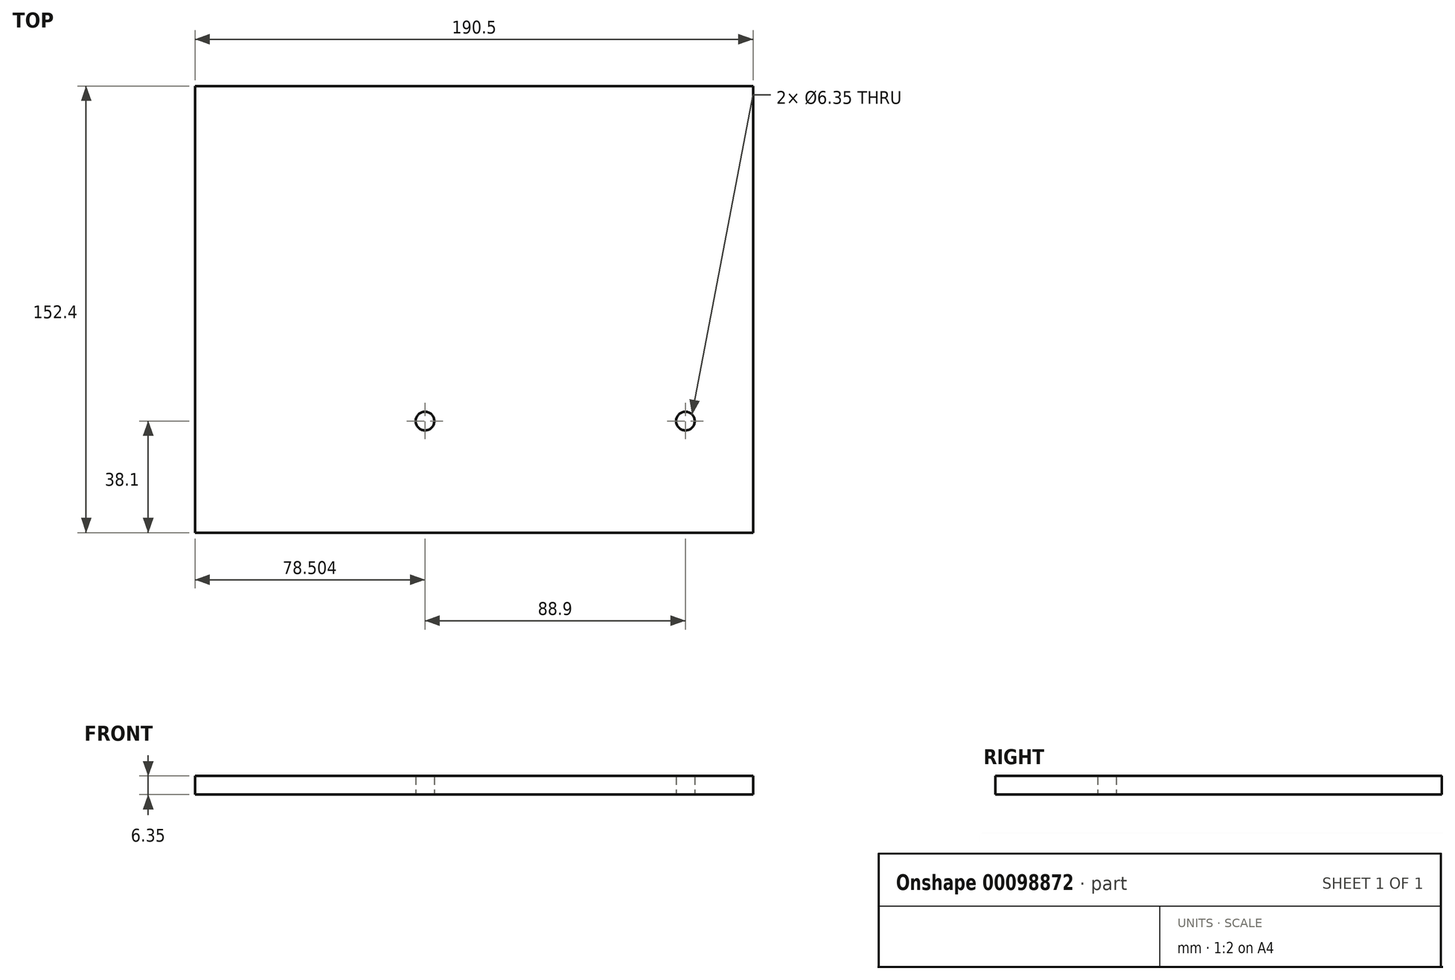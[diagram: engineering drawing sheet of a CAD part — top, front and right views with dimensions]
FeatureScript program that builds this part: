
annotation { "Feature Type Name" : "Feature", "Feature Type Description" : "" }
export const myFeature = defineFeature(function(context is Context, id is Id, definition is map)
    precondition{}
    {
        {
            var Q0;
            Q0=qCreatedBy(makeId("Top.planeOp"),FACE);
            var sketch = newSketch(context, id + "F0", { "sketchPlane" : qUnion([Q0])});
            skLineSegment(sketch, "E0.bottom", {"start": v(95.25, 76.2) * mm, "end": v(-95.25, 76.2) * mm});
            skLineSegment(sketch, "E0.top", {"start": v(95.25, -76.2) * mm, "end": v(-95.25, -76.2) * mm});
            skLineSegment(sketch, "E0.left", {"start": v(95.25, 76.2) * mm, "end": v(95.25, -76.2) * mm});
            skLineSegment(sketch, "E0.right", {"start": v(-95.25, 76.2) * mm, "end": v(-95.25, -76.2) * mm});
            skPoint(sketch, "E0.middle", {"position": v(0, 0) * mm});
            skCircle(sketch, "E1", {"center": v(-16.75, -38.1) * mm, "radius": 3.18 * mm});
            skCircle(sketch, "E2.1.0.0", {"center": v(72.15, -38.1) * mm, "radius": 3.18 * mm});
            skLineSegment(sketch, "E2.direction1", {"start": v(-16.75, -38.1) * mm, "end": v(72.15, -38.1) * mm, "construction": true});
            skSolve(sketch);
        }
        {
            var Q0;
            Q0 = qSketchRegion(id + "F0", true);
            extrude(context, id + "F1", {"entities" : qUnion([Q0]), "depth" : 6.35 * mm});
        }
    });
